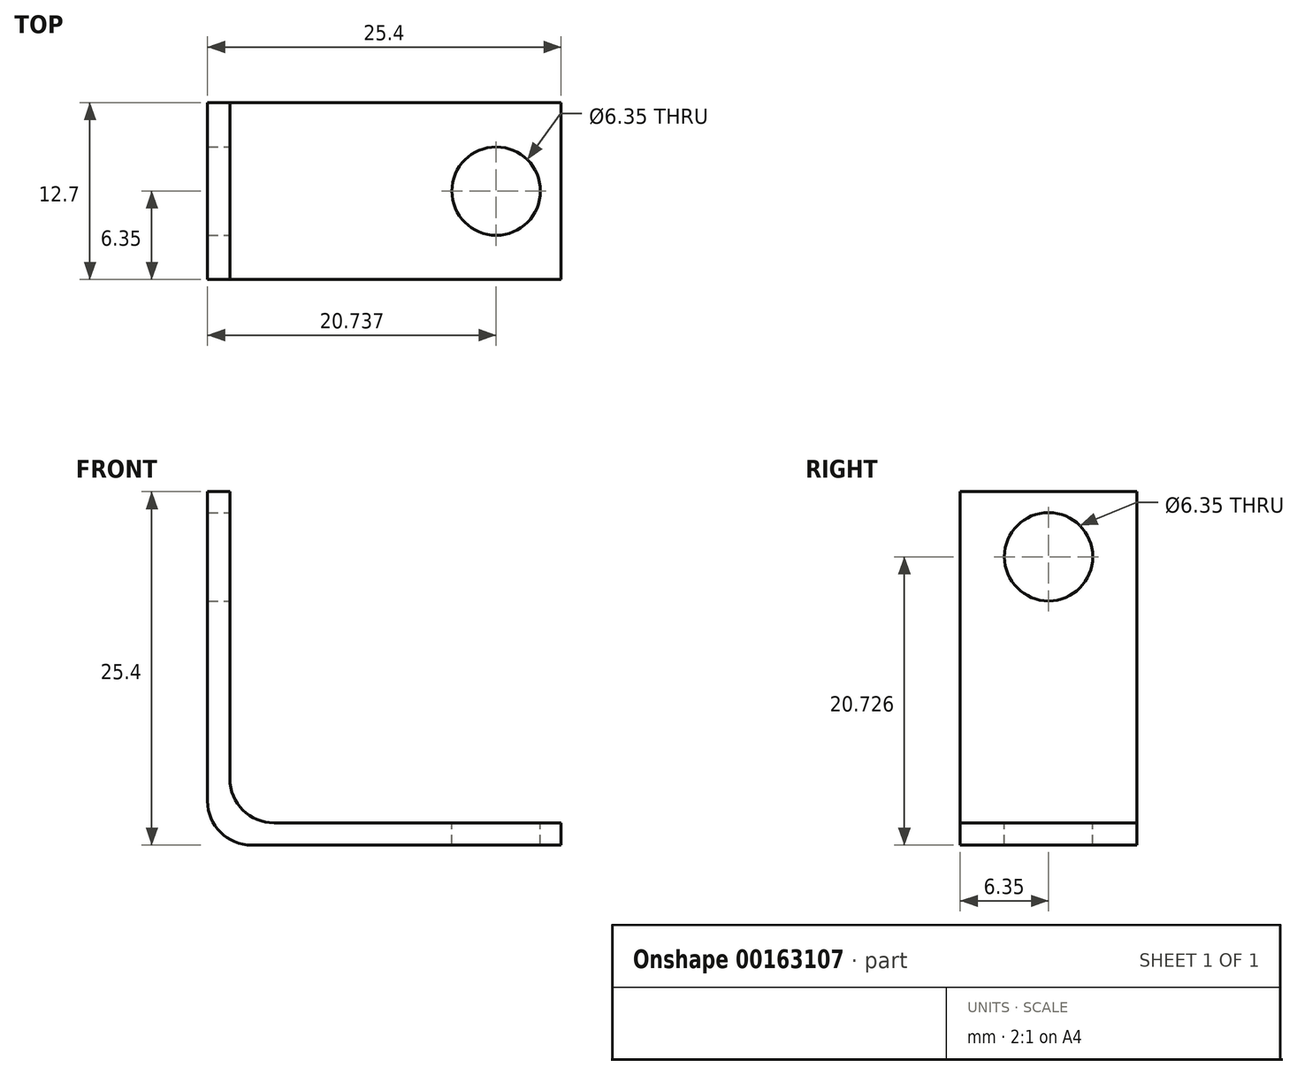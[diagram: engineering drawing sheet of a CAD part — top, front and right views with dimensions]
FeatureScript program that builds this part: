
annotation { "Feature Type Name" : "Feature", "Feature Type Description" : "" }
export const myFeature = defineFeature(function(context is Context, id is Id, definition is map)
    precondition{}
    {
        {
            var Q0;
            Q0=qCreatedBy(makeId("Front.planeOp"),FACE);
            var sketch = newSketch(context, id + "F0", { "sketchPlane" : qUnion([Q0])});
            skLineSegment(sketch, "E0", {"start": v(0, 3.18) * mm, "end": v(0, 25.4) * mm});
            skLineSegment(sketch, "E1", {"start": v(0, 25.4) * mm, "end": v(1.6, 25.4) * mm});
            skLineSegment(sketch, "E2", {"start": v(1.6, 25.4) * mm, "end": v(1.6, 4.78) * mm});
            skLineSegment(sketch, "E3", {"start": v(3.18, 0) * mm, "end": v(25.4, 0) * mm});
            skLineSegment(sketch, "E4", {"start": v(25.4, 0) * mm, "end": v(25.4, 1.6) * mm});
            skLineSegment(sketch, "E5", {"start": v(25.4, 1.6) * mm, "end": v(4.78, 1.6) * mm});
            skPoint(sketch, "E6.orphan", {"position": v(1.6, 0) * mm});
            skPoint(sketch, "E7.visualSharp", {"position": v(1.6, 1.6) * mm});
            skArc(sketch, "E7.filletArc", {"start": v(1.6, 4.78) * mm, "mid": v(2.53, 2.53) * mm, "end": v(4.78, 1.6) * mm});
            skPoint(sketch, "E8.visualSharp", {"position": v(0, 0) * mm});
            skArc(sketch, "E8.filletArc", {"start": v(0, 3.18) * mm, "mid": v(0.93, 0.93) * mm, "end": v(3.18, 0) * mm});
            skSolve(sketch);
        }
        {
            var Q0;
            Q0 = qSketchRegion(id + "F0", true);
            extrude(context, id + "F1", {"entities" : qUnion([Q0]), "depth" : 12.7 * mm});
        }
        {
            var Q0;
            Q0=makeQuery(id+"F1.opExtrude","SWEPT_FACE",FACE,{"disambiguationData":[OSD([sQuery(id+"F0.wireOp",EDGE,"E5")])]});
            var sketch = newSketch(context, id + "F2", { "sketchPlane" : qUnion([Q0])});
            skCircle(sketch, "E9", {"center": v(20.74, -6.35) * mm, "radius": 3.18 * mm});
            skSolve(sketch);
        }
        {
            var Q0;
            Q0 = qSketchRegion(id + "F2", true);
            extrude(context, id + "F3", {"entities" : qUnion([Q0]), "operationType" : NewBodyOperationType.REMOVE, "oppositeDirection" : true, "depth" : 25.4 * mm});
        }
        {
            var Q0;
            Q0=makeQuery(id+"F1.opExtrude","SWEPT_FACE",FACE,{"disambiguationData":[OSD([sQuery(id+"F0.wireOp",EDGE,"E2")])]});
            var sketch = newSketch(context, id + "F4", { "sketchPlane" : qUnion([Q0])});
            skCircle(sketch, "E10", {"center": v(-6.35, 20.73) * mm, "radius": 3.18 * mm});
            skSolve(sketch);
        }
        {
            var Q0;
            Q0 = qSketchRegion(id + "F4", true);
            extrude(context, id + "F5", {"entities" : qUnion([Q0]), "operationType" : NewBodyOperationType.REMOVE, "oppositeDirection" : true, "depth" : 25.4 * mm});
        }
    });
